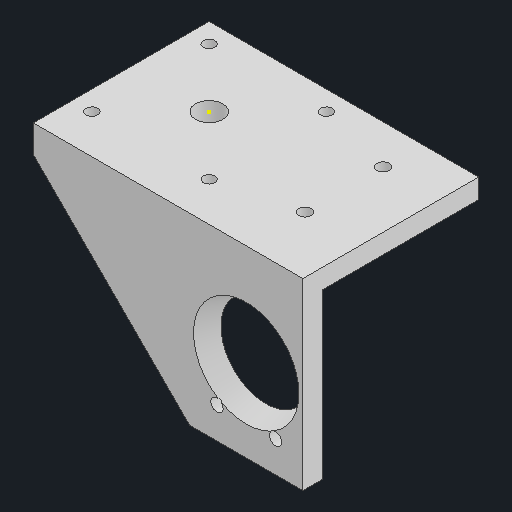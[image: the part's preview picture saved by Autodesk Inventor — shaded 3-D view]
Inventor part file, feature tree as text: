
AUTODESK INVENTOR PART (.ipt)
format: ipt  version: 2025.1 (Build 291241000, 241)  size: 386,048 bytes
history: native  units: mm
features: sketch x3, extrude x3, chamfer x2, projected_geometry x1
ambient origin geometry x8: Origin, YZ Plane, XZ Plane, XY Plane, X Axis, Y Axis, Z Axis, Center Point
bodies: Solid1 (feature_tree)
feature tree (9):
  sketch  "Sketch1"  dims[d0=40.0mm d1=40.0mm]
  extrude  "Extrusion1"  Depth=40.0mm
  extrude  "Extrusion4"  Depth=3.0mm
  extrude  "Extrusion5"  Depth=10.0mm
  chamfer  "Chamfer4"  Distance=29.0mm
  chamfer  "Chamfer5"  Distance=5.0mm
  sketch  "Sketch3"  dims[d8=5.0mm d9=0.0mm d26=7.0mm d27=29.0mm d29=5.0mm d30=42.0mm d31=0.0mm d32=29.0mm d33=21.0mm d34=23.0mm d35=42.0mm d36=0.0mm d37=3.2mm d39=8.0mm d40=10.0mm d41=20.0mm d42=3.2mm d43=40.0mm d44=2.0mm d45=45.0deg d46=15.0mm d47=2.0mm d48=5.0mm d49=45.0deg d28=0.872665mm]
  sketch  "Sketch2"  dims[d2=30.0mm d3=3.0mm]
  projected_geometry  "Projected Loop1"
